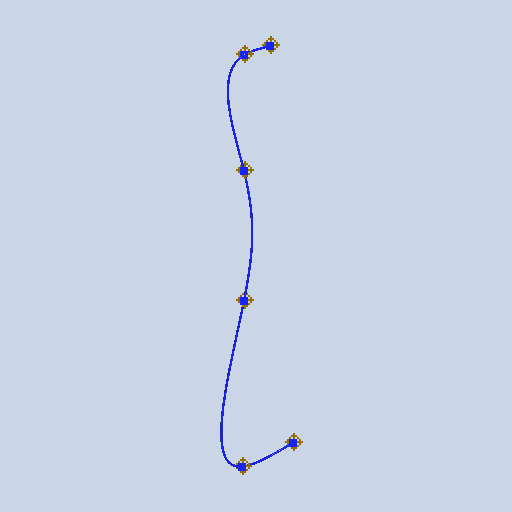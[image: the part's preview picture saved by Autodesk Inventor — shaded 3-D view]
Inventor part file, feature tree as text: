
AUTODESK INVENTOR PART (.ipt)
format: ipt  version: 2025 (Build 290162000, 162)  size: 152,576 bytes
history: native  units: mm (DEFAULTED — no unit token found)
features: other x8, plane x1, sketch x1, sweep x1
ambient origin geometry x8: Origin, YZ Plane, XZ Plane, XY Plane, X Axis, Y Axis, Z Axis, Center Point
bodies: Body1 (feature_tree)
feature tree (11):
  other  "Work Point1"
  other  "Work Point2"
  other  "Segment1"
  other  "Work Point3"
  other  "Work Point4"
  other  "Work Point5"
  other  "Work Point6"
  plane  "Work Plane1"
  sketch  "Sketch1"  dims[d0=0.0mm d1=0.0mm]
  other  "Srf1"
  sweep  "SweepSrf1"
